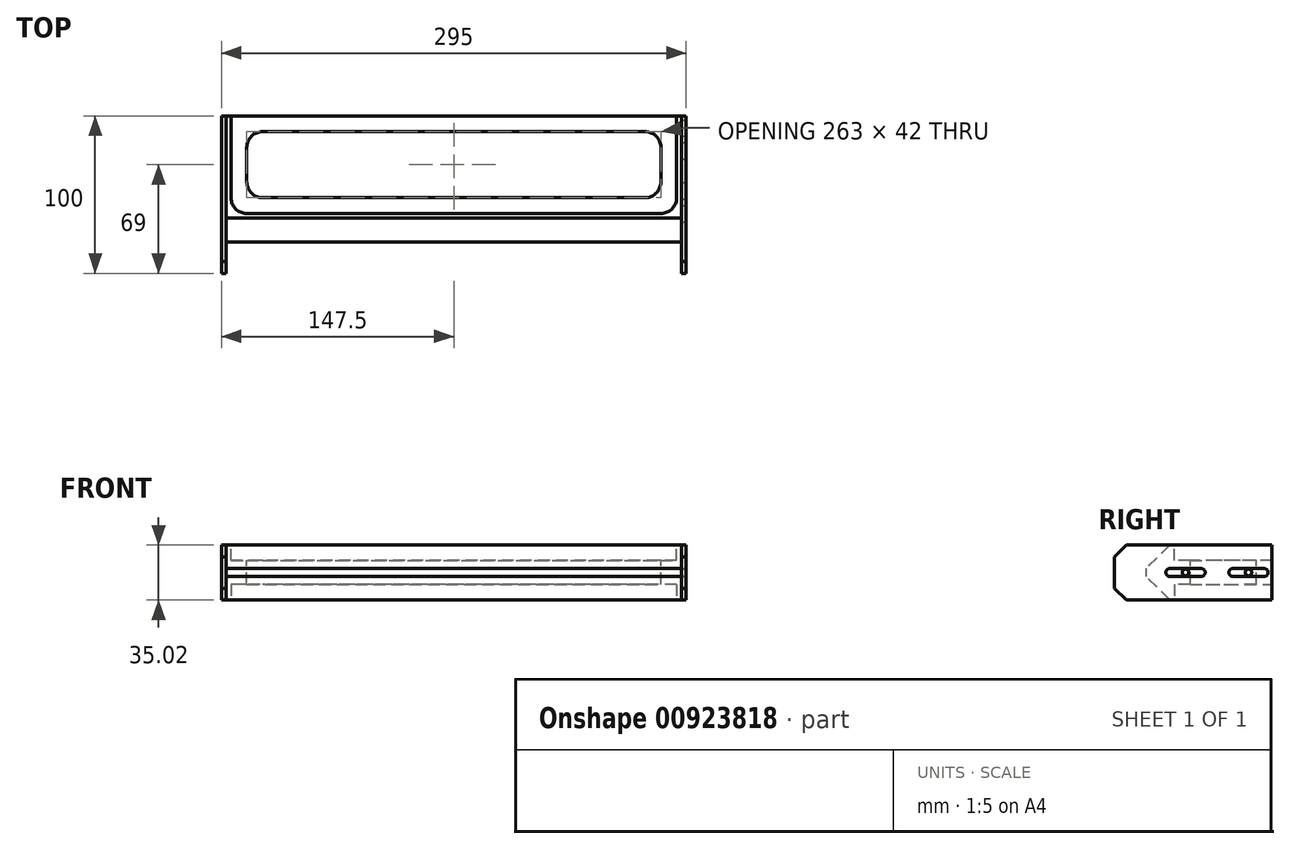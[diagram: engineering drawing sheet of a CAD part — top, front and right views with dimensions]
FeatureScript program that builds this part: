
annotation { "Feature Type Name" : "Feature", "Feature Type Description" : "" }
export const myFeature = defineFeature(function(context is Context, id is Id, definition is map)
    precondition{}
    {
        {
            var Q0;
            Q0=qCreatedBy(makeId("Top.planeOp"),FACE);
            var sketch = newSketch(context, id + "F0", { "sketchPlane" : qUnion([Q0])});
            skLineSegment(sketch, "E0.bottom", {"start": v(147.5, 50) * mm, "end": v(-147.5, 50) * mm});
            skLineSegment(sketch, "E0.top", {"start": v(147.5, -50) * mm, "end": v(144.5, -50) * mm});
            skLineSegment(sketch, "E0.left", {"start": v(147.5, 50) * mm, "end": v(147.5, -50) * mm});
            skLineSegment(sketch, "E0.right", {"start": v(-147.5, 50) * mm, "end": v(-147.5, -50) * mm});
            skPoint(sketch, "E0.middle", {"position": v(0, 0) * mm});
            skLineSegment(sketch, "E1", {"start": v(-144.5, -50) * mm, "end": v(-144.5, -30) * mm});
            skLineSegment(sketch, "E2", {"start": v(-144.5, -30) * mm, "end": v(144.5, -30) * mm});
            skLineSegment(sketch, "E3", {"start": v(144.5, -30) * mm, "end": v(144.5, -50) * mm});
            skLineSegment(sketch, "E4.trimOffspring", {"start": v(-144.5, -50) * mm, "end": v(-147.5, -50) * mm});
            skSolve(sketch);
        }
        {
            var Q0;
            Q0=qSketchRegion(id+"F0",true);
            extrude(context, id + "F1", {"entities" : qUnion([Q0]), "depth" : 17.5 * mm, "offsetDistance" : 25 * mm, "hasSecondDirection" : true, "secondDirectionOppositeDirection" : true, "secondDirectionDepth" : 17.5 * mm});
        }
        {
            var Q0;
            Q0=makeQuery(id+"F1.opExtrude","CAP_EDGE",EDGE,{"disambiguationData":[OSD([sQuery(id+"F0.wireOp",EDGE,"E2")])],"isStart":false});
            var Q1;
            Q1=makeQuery(id+"F1.opExtrude","CAP_EDGE",EDGE,{"disambiguationData":[OSD([sQuery(id+"F0.wireOp",EDGE,"E2")])],"isStart":true});
            chamfer(context, id + "F2", {"entities" : qUnion([Q0, Q1]), "width" : 15 * mm, "tangentPropagation" : true});
        }
        {
            var Q0;
            Q0=makeQuery(id+"F1.opExtrude","CAP_EDGE",EDGE,{"disambiguationData":[OSD([sQuery(id+"F0.wireOp",EDGE,"E0.top")])],"isStart":false});
            var Q1;
            Q1=makeQuery(id+"F1.opExtrude","CAP_EDGE",EDGE,{"disambiguationData":[OSD([sQuery(id+"F0.wireOp",EDGE,"E0.top")])],"isStart":true});
            var Q2;
            Q2=makeQuery(id+"F1.opExtrude","CAP_EDGE",EDGE,{"disambiguationData":[OSD([sQuery(id+"F0.wireOp",EDGE,"E4.trimOffspring")])],"isStart":false});
            var Q3;
            Q3=makeQuery(id+"F1.opExtrude","CAP_EDGE",EDGE,{"disambiguationData":[OSD([sQuery(id+"F0.wireOp",EDGE,"E4.trimOffspring")])],"isStart":true});
            chamfer(context, id + "F3", {"entities" : qUnion([Q0, Q1, Q2, Q3]), "width" : 7.5 * mm, "tangentPropagation" : true});
        }
        {
            var Q0;
            Q0=makeQuery(id+"F1.opExtrude","SWEPT_FACE",FACE,{"disambiguationData":[OSD([sQuery(id+"F0.wireOp",EDGE,"E0.left")])]});
            var sketch = newSketch(context, id + "F4", { "sketchPlane" : qUnion([Q0])});
            skLineSegment(sketch, "E5.bottom", {"start": v(45, 2.5) * mm, "end": v(25, 2.5) * mm});
            skLineSegment(sketch, "E5.top", {"start": v(45, -2.5) * mm, "end": v(25, -2.5) * mm});
            skLineSegment(sketch, "E5.left", {"start": v(47.5, 0) * mm, "end": v(47.5, 0) * mm});
            skLineSegment(sketch, "E5.right", {"start": v(22.5, 0) * mm, "end": v(22.5, 0) * mm});
            skLineSegment(sketch, "E6.bottom", {"start": v(5, 2.5) * mm, "end": v(-15, 2.5) * mm});
            skLineSegment(sketch, "E6.top", {"start": v(5, -2.5) * mm, "end": v(-15, -2.5) * mm});
            skLineSegment(sketch, "E6.left", {"start": v(7.5, 0) * mm, "end": v(7.5, 0) * mm});
            skLineSegment(sketch, "E6.right", {"start": v(-17.5, 0) * mm, "end": v(-17.5, 0) * mm});
            skPoint(sketch, "E7.visualSharp", {"position": v(-17.5, 2.5) * mm});
            skArc(sketch, "E7.filletArc", {"start": v(-15, 2.5) * mm, "mid": v(-16.77, 1.77) * mm, "end": v(-17.5, 0) * mm});
            skPoint(sketch, "E8.visualSharp", {"position": v(-17.5, -2.5) * mm});
            skArc(sketch, "E8.filletArc", {"start": v(-17.5, 0) * mm, "mid": v(-16.77, -1.77) * mm, "end": v(-15, -2.5) * mm});
            skPoint(sketch, "E9.visualSharp", {"position": v(7.5, 2.5) * mm});
            skArc(sketch, "E9.filletArc", {"start": v(7.5, 0) * mm, "mid": v(6.77, 1.77) * mm, "end": v(5, 2.5) * mm});
            skPoint(sketch, "E10.visualSharp", {"position": v(7.5, -2.5) * mm});
            skArc(sketch, "E10.filletArc", {"start": v(5, -2.5) * mm, "mid": v(6.77, -1.77) * mm, "end": v(7.5, 0) * mm});
            skPoint(sketch, "E11.visualSharp", {"position": v(22.5, 2.5) * mm});
            skArc(sketch, "E11.filletArc", {"start": v(25, 2.5) * mm, "mid": v(23.23, 1.77) * mm, "end": v(22.5, 0) * mm});
            skPoint(sketch, "E12.visualSharp", {"position": v(22.5, -2.5) * mm});
            skArc(sketch, "E12.filletArc", {"start": v(22.5, 0) * mm, "mid": v(23.23, -1.77) * mm, "end": v(25, -2.5) * mm});
            skPoint(sketch, "E13.visualSharp", {"position": v(47.5, 2.5) * mm});
            skArc(sketch, "E13.filletArc", {"start": v(47.5, 0) * mm, "mid": v(46.77, 1.77) * mm, "end": v(45, 2.5) * mm});
            skPoint(sketch, "E14.visualSharp", {"position": v(47.5, -2.5) * mm});
            skArc(sketch, "E14.filletArc", {"start": v(45, -2.5) * mm, "mid": v(46.77, -1.77) * mm, "end": v(47.5, 0) * mm});
            skCircle(sketch, "E15", {"center": v(-5, 0) * mm, "radius": 2.1 * mm});
            skCircle(sketch, "E16", {"center": v(35, 0) * mm, "radius": 2.1 * mm});
            skPoint(sketch, "E16.centerSnap0", {"position": v(35, -2.5) * mm});
            skLineSegment(sketch, "E17", {"start": v(-50, 0) * mm, "end": v(50, 0) * mm, "construction": true});
            skSolve(sketch);
        }
        {
            var Q0;
            Q0=makeQuery(id+"F1.opExtrude","CAP_FACE",FACE,{"disambiguationData":[OSD([sQuery(id+"F0.wireOp",EDGE,"E0.bottom"),sQuery(id+"F0.wireOp",EDGE,"E0.top"),sQuery(id+"F0.wireOp",EDGE,"E0.left"),sQuery(id+"F0.wireOp",EDGE,"E0.right"),sQuery(id+"F0.wireOp",EDGE,"E1"),sQuery(id+"F0.wireOp",EDGE,"E2"),sQuery(id+"F0.wireOp",EDGE,"E3"),sQuery(id+"F0.wireOp",EDGE,"E4.trimOffspring")])],"isStart":false});
            var sketch = newSketch(context, id + "F5", { "sketchPlane" : qUnion([Q0])});
            skLineSegment(sketch, "E18.bottom", {"start": v(-147.5, 50) * mm, "end": v(-144.5, 50) * mm});
            skLineSegment(sketch, "E18.top", {"start": v(-147.5, -42.5) * mm, "end": v(-144.5, -42.5) * mm});
            skLineSegment(sketch, "E18.left", {"start": v(-147.5, 50) * mm, "end": v(-147.5, -42.5) * mm});
            skLineSegment(sketch, "E18.right", {"start": v(-144.5, 50) * mm, "end": v(-144.5, -42.5) * mm});
            skLineSegment(sketch, "E19.bottom", {"start": v(147.5, 50) * mm, "end": v(144.5, 50) * mm});
            skLineSegment(sketch, "E19.top", {"start": v(147.5, -42.5) * mm, "end": v(144.5, -42.5) * mm});
            skLineSegment(sketch, "E19.left", {"start": v(147.5, 50) * mm, "end": v(147.5, -42.5) * mm});
            skLineSegment(sketch, "E19.right", {"start": v(144.5, 50) * mm, "end": v(144.5, -42.5) * mm});
            skSolve(sketch);
        }
        {
            var Q0;
            Q0=qSketchRegion(id+"F5",true);
            extrude(context, id + "F6", {"entities" : qUnion([Q0]), "operationType" : NewBodyOperationType.ADD, "depth" : 0.01 * mm, "offsetDistance" : 25 * mm});
        }
        {
            var Q0;
            Q0=makeQuery(id+"F1.opExtrude","CAP_FACE",FACE,{"disambiguationData":[OSD([sQuery(id+"F0.wireOp",EDGE,"E0.bottom"),sQuery(id+"F0.wireOp",EDGE,"E0.top"),sQuery(id+"F0.wireOp",EDGE,"E0.left"),sQuery(id+"F0.wireOp",EDGE,"E0.right"),sQuery(id+"F0.wireOp",EDGE,"E1"),sQuery(id+"F0.wireOp",EDGE,"E2"),sQuery(id+"F0.wireOp",EDGE,"E3"),sQuery(id+"F0.wireOp",EDGE,"E4.trimOffspring")])],"isStart":true});
            var sketch = newSketch(context, id + "F7", { "sketchPlane" : qUnion([Q0])});
            skLineSegment(sketch, "E20.bottom", {"start": v(-147.5, -50) * mm, "end": v(-144.5, -50) * mm});
            skLineSegment(sketch, "E20.top", {"start": v(-147.5, 42.5) * mm, "end": v(-144.5, 42.5) * mm});
            skLineSegment(sketch, "E20.left", {"start": v(-147.5, -50) * mm, "end": v(-147.5, 42.5) * mm});
            skLineSegment(sketch, "E20.right", {"start": v(-144.5, -50) * mm, "end": v(-144.5, 42.5) * mm});
            skLineSegment(sketch, "E21.bottom", {"start": v(147.5, -50) * mm, "end": v(144.5, -50) * mm});
            skLineSegment(sketch, "E21.top", {"start": v(147.5, 42.5) * mm, "end": v(144.5, 42.5) * mm});
            skLineSegment(sketch, "E21.left", {"start": v(147.5, -50) * mm, "end": v(147.5, 42.5) * mm});
            skLineSegment(sketch, "E21.right", {"start": v(144.5, -50) * mm, "end": v(144.5, 42.5) * mm});
            skSolve(sketch);
        }
        {
            var Q0;
            Q0=qSketchRegion(id+"F7",true);
            extrude(context, id + "F8", {"entities" : qUnion([Q0]), "operationType" : NewBodyOperationType.ADD, "depth" : 0.01 * mm, "offsetDistance" : 25 * mm});
        }
        {
            var Q0;
            Q0=makeQuery(id+"F4.imprint","IMPRINT",FACE,{"disambiguationData":[TD([[makeQuery(id+"F4.imprint","IMPRINT",EDGE,{"derivedFrom":sQuery(id+"F4.wireOp",EDGE,"E5.bottom")}),1.0]])]});
            var Q1;
            Q1=makeQuery(id+"F4.imprint","IMPRINT",FACE,{"disambiguationData":[TD([[makeQuery(id+"F4.imprint","IMPRINT",EDGE,{"derivedFrom":sQuery(id+"F4.wireOp",EDGE,"E6.bottom")}),1.0]])]});
            extrude(context, id + "F9", {"entities" : qUnion([Q0, Q1]), "operationType" : NewBodyOperationType.REMOVE, "oppositeDirection" : true, "depth" : 3 * mm, "offsetDistance" : 25 * mm});
        }
        {
            var Q0;
            Q0=makeQuery(id+"F1.opExtrude","CAP_FACE",FACE,{"disambiguationData":[OSD([sQuery(id+"F0.wireOp",EDGE,"E0.bottom"),sQuery(id+"F0.wireOp",EDGE,"E0.top"),sQuery(id+"F0.wireOp",EDGE,"E0.left"),sQuery(id+"F0.wireOp",EDGE,"E0.right"),sQuery(id+"F0.wireOp",EDGE,"E1"),sQuery(id+"F0.wireOp",EDGE,"E2"),sQuery(id+"F0.wireOp",EDGE,"E3"),sQuery(id+"F0.wireOp",EDGE,"E4.trimOffspring")])],"isStart":false});
            var sketch = newSketch(context, id + "F10", { "sketchPlane" : qUnion([Q0])});
            skLineSegment(sketch, "E22.bottom", {"start": v(-141.5, 50) * mm, "end": v(141.5, 50) * mm});
            skLineSegment(sketch, "E22.top", {"start": v(-131.5, -12) * mm, "end": v(131.5, -12) * mm});
            skLineSegment(sketch, "E22.left", {"start": v(-141.5, 50) * mm, "end": v(-141.5, -2) * mm});
            skLineSegment(sketch, "E22.right", {"start": v(141.5, 50) * mm, "end": v(141.5, -2) * mm});
            skPoint(sketch, "E23.visualSharp", {"position": v(-141.5, -12) * mm});
            skArc(sketch, "E23.filletArc", {"start": v(-141.5, -2) * mm, "mid": v(-138.57, -9.07) * mm, "end": v(-131.5, -12) * mm});
            skPoint(sketch, "E24.visualSharp", {"position": v(141.5, -12) * mm});
            skArc(sketch, "E24.filletArc", {"start": v(131.5, -12) * mm, "mid": v(138.57, -9.07) * mm, "end": v(141.5, -2) * mm});
            skSolve(sketch);
        }
        {
            var Q0;
            Q0=makeQuery(id+"F10.imprint","IMPRINT",FACE,{"disambiguationData":[TD([[makeQuery(id+"F10.imprint","IMPRINT",EDGE,{"derivedFrom":sQuery(id+"F10.wireOp",EDGE,"E22.bottom")}),1.0]])]});
            extrude(context, id + "F11", {"entities" : qUnion([Q0]), "operationType" : NewBodyOperationType.REMOVE, "oppositeDirection" : true, "depth" : 10 * mm, "offsetDistance" : 25 * mm});
        }
        {
            var Q0;
            Q0=makeQuery(id+"F1.opExtrude","CAP_FACE",FACE,{"disambiguationData":[OSD([sQuery(id+"F0.wireOp",EDGE,"E0.bottom"),sQuery(id+"F0.wireOp",EDGE,"E0.top"),sQuery(id+"F0.wireOp",EDGE,"E0.left"),sQuery(id+"F0.wireOp",EDGE,"E0.right"),sQuery(id+"F0.wireOp",EDGE,"E1"),sQuery(id+"F0.wireOp",EDGE,"E2"),sQuery(id+"F0.wireOp",EDGE,"E3"),sQuery(id+"F0.wireOp",EDGE,"E4.trimOffspring")])],"isStart":true});
            var sketch = newSketch(context, id + "F12", { "sketchPlane" : qUnion([Q0])});
            skLineSegment(sketch, "E25.0.0", {"start": v(141.5, 2) * mm, "end": v(141.5, -50) * mm});
            skLineSegment(sketch, "E25.0.1", {"start": v(141.5, -50) * mm, "end": v(-141.5, -50) * mm});
            skLineSegment(sketch, "E25.0.2", {"start": v(-141.5, -50) * mm, "end": v(-141.5, 2) * mm});
            skArc(sketch, "E25.0.3", {"start": v(-141.5, 2) * mm, "mid": v(-138.57, 9.07) * mm, "end": v(-131.5, 12) * mm});
            skLineSegment(sketch, "E25.0.4", {"start": v(-131.5, 12) * mm, "end": v(131.5, 12) * mm});
            skArc(sketch, "E25.0.5", {"start": v(131.5, 12) * mm, "mid": v(138.57, 9.07) * mm, "end": v(141.5, 2) * mm});
            skSolve(sketch);
        }
        {
            var Q0;
            Q0=qSketchRegion(id+"F12",true);
            extrude(context, id + "F13", {"entities" : qUnion([Q0]), "operationType" : NewBodyOperationType.REMOVE, "oppositeDirection" : true, "depth" : 10 * mm, "offsetDistance" : 25 * mm});
        }
        {
            var Q0;
            Q0=makeQuery(id+"F11.boolean.opBoolean","COPY",FACE,{"derivedFrom":makeQuery(id+"F11.opExtrude","CAP_FACE",FACE,{"disambiguationData":[OSD([sQuery(id+"F10.wireOp",EDGE,"E22.bottom"),sQuery(id+"F10.wireOp",EDGE,"E22.top"),sQuery(id+"F10.wireOp",EDGE,"E22.left"),sQuery(id+"F10.wireOp",EDGE,"E22.right"),sQuery(id+"F10.wireOp",EDGE,"E23.filletArc"),sQuery(id+"F10.wireOp",EDGE,"E24.filletArc")])],"isStart":false})});
            var sketch = newSketch(context, id + "F14", { "sketchPlane" : qUnion([Q0])});
            skLineSegment(sketch, "E26.bottom", {"start": v(-121.5, 40) * mm, "end": v(121.5, 40) * mm});
            skLineSegment(sketch, "E26.top", {"start": v(-121.5, -2) * mm, "end": v(121.5, -2) * mm});
            skLineSegment(sketch, "E26.left", {"start": v(-131.5, 30) * mm, "end": v(-131.5, 8) * mm});
            skLineSegment(sketch, "E26.right", {"start": v(131.5, 30) * mm, "end": v(131.5, 8) * mm});
            skPoint(sketch, "E27.visualSharp", {"position": v(-131.5, 40) * mm});
            skArc(sketch, "E27.filletArc", {"start": v(-121.5, 40) * mm, "mid": v(-128.57, 37.07) * mm, "end": v(-131.5, 30) * mm});
            skPoint(sketch, "E28.visualSharp", {"position": v(-131.5, -2) * mm});
            skArc(sketch, "E28.filletArc", {"start": v(-131.5, 8) * mm, "mid": v(-128.57, 0.93) * mm, "end": v(-121.5, -2) * mm});
            skPoint(sketch, "E29.visualSharp", {"position": v(131.5, 40) * mm});
            skArc(sketch, "E29.filletArc", {"start": v(131.5, 30) * mm, "mid": v(128.57, 37.07) * mm, "end": v(121.5, 40) * mm});
            skPoint(sketch, "E30.visualSharp", {"position": v(131.5, -2) * mm});
            skArc(sketch, "E30.filletArc", {"start": v(121.5, -2) * mm, "mid": v(128.57, 0.93) * mm, "end": v(131.5, 8) * mm});
            skSolve(sketch);
        }
        {
            var Q0;
            Q0=makeQuery(id+"F14.imprint","IMPRINT",FACE,{"disambiguationData":[TD([[makeQuery(id+"F14.imprint","IMPRINT",EDGE,{"derivedFrom":sQuery(id+"F14.wireOp",EDGE,"E26.bottom")}),-1.0]])]});
            extrude(context, id + "F15", {"entities" : qUnion([Q0]), "operationType" : NewBodyOperationType.REMOVE, "oppositeDirection" : true, "depth" : 25 * mm, "offsetDistance" : 25 * mm});
        }
    });
